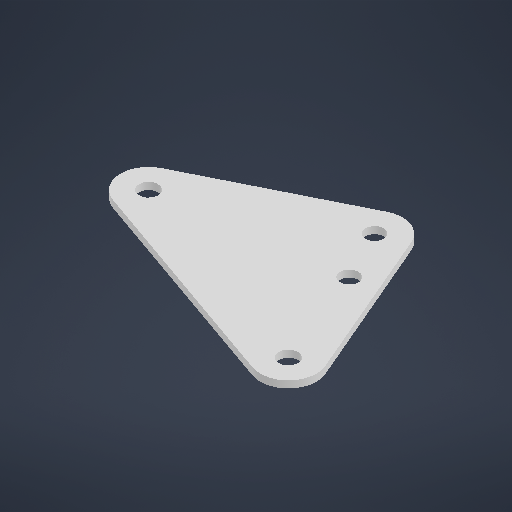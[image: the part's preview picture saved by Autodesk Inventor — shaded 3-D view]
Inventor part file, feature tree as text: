
AUTODESK INVENTOR PART (.ipt)
format: ipt  version: 2025.2 (Build 292293000, 293)  size: 193,024 bytes
history: native  units: in
note: dims shown in document units (in); Inventor stores cm internally (conversion verified against a paired STEP export)
features: extrude x1, sketch x1
ambient origin geometry x8: Origin, YZ Plane, XZ Plane, XY Plane, X Axis, Y Axis, Z Axis, Center Point
bodies: Solid1 (feature_tree)
feature tree (2):
  extrude  "Extrusion1"  Depth=0.0625in
  sketch  "Sketch1"  dims[d0=0.5in d1=0.5in d3=0.5in d4=0.0625in d5=0.0in]
